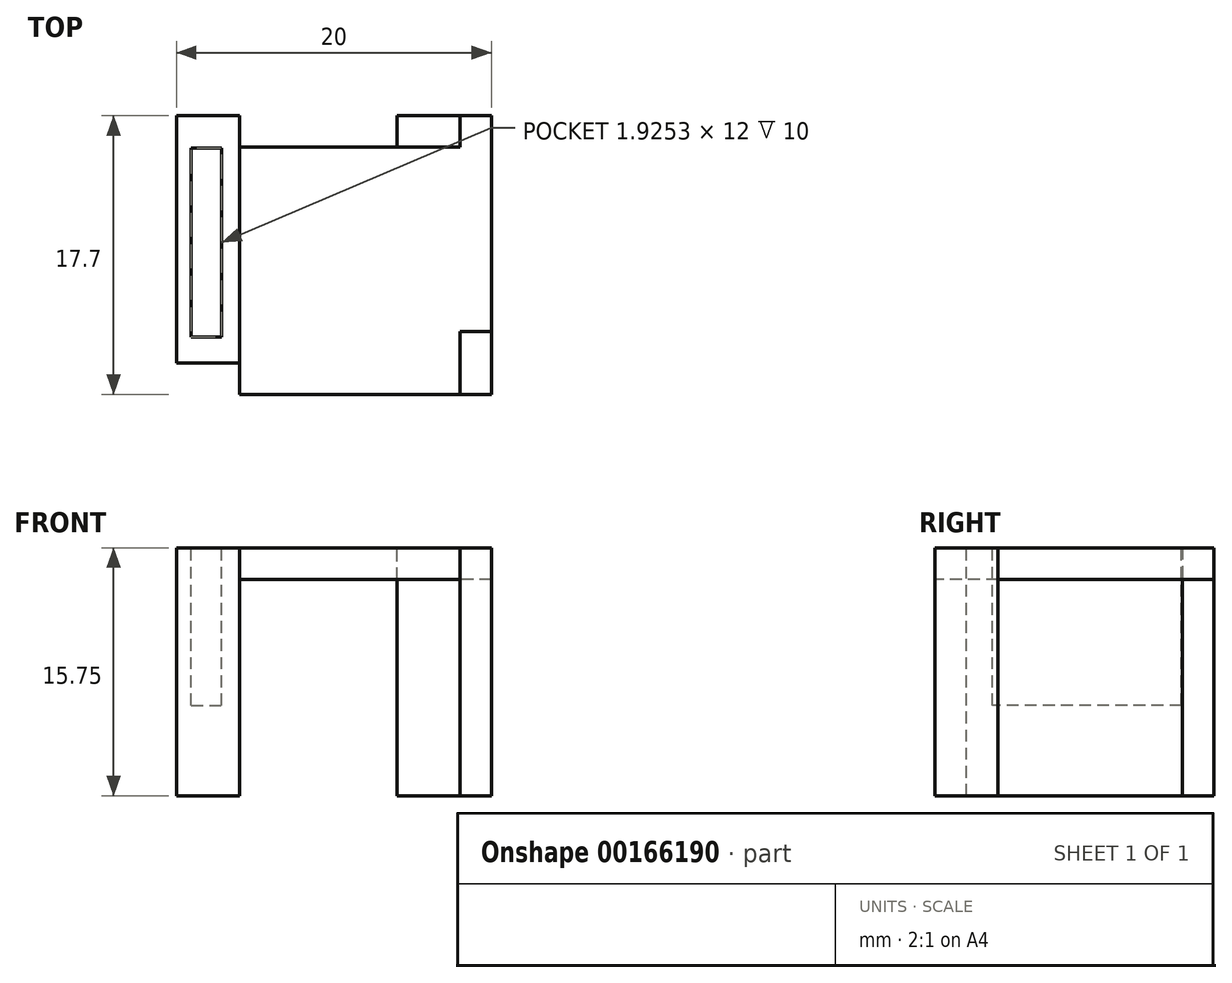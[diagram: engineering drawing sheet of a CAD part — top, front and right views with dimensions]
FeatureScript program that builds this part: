
annotation { "Feature Type Name" : "Feature", "Feature Type Description" : "" }
export const myFeature = defineFeature(function(context is Context, id is Id, definition is map)
    precondition{}
    {
        {
            var Q0;
            Q0=qCreatedBy(makeId("Top.planeOp"),FACE);
            var sketch = newSketch(context, id + "F0", { "sketchPlane" : qUnion([Q0])});
            skLineSegment(sketch, "E0", {"start": v(41.87, -13.52) * mm, "end": v(43.87, -13.52) * mm});
            skLineSegment(sketch, "E1", {"start": v(43.87, -13.52) * mm, "end": v(43.87, -9.52) * mm});
            skLineSegment(sketch, "E2", {"start": v(43.87, -9.52) * mm, "end": v(41.87, -9.52) * mm});
            skLineSegment(sketch, "E3", {"start": v(41.87, -9.52) * mm, "end": v(41.87, -13.52) * mm});
            skLineSegment(sketch, "E4", {"start": v(43.87, -9.52) * mm, "end": v(43.87, 4.18) * mm});
            skLineSegment(sketch, "E5", {"start": v(43.87, 4.18) * mm, "end": v(41.87, 4.18) * mm});
            skLineSegment(sketch, "E6", {"start": v(41.87, 4.18) * mm, "end": v(41.87, 2.18) * mm});
            skLineSegment(sketch, "E7", {"start": v(41.87, 2.18) * mm, "end": v(27.87, 2.18) * mm});
            skLineSegment(sketch, "E8", {"start": v(41.87, -13.52) * mm, "end": v(27.87, -13.52) * mm});
            skLineSegment(sketch, "E9", {"start": v(27.87, 2.18) * mm, "end": v(27.87, -13.52) * mm});
            skLineSegment(sketch, "E10", {"start": v(41.87, 4.18) * mm, "end": v(37.87, 4.18) * mm});
            skLineSegment(sketch, "E11", {"start": v(37.87, 4.18) * mm, "end": v(37.87, 2.18) * mm});
            skLineSegment(sketch, "E12", {"start": v(37.87, 4.18) * mm, "end": v(23.87, 4.18) * mm});
            skLineSegment(sketch, "E13", {"start": v(27.87, -11.52) * mm, "end": v(23.87, -11.52) * mm});
            skPoint(sketch, "E14.orphan", {"position": v(41.87, -11.52) * mm});
            skLineSegment(sketch, "E15", {"start": v(23.87, -11.52) * mm, "end": v(23.87, 4.18) * mm});
            skLineSegment(sketch, "E16", {"start": v(27.87, 2.18) * mm, "end": v(27.87, 4.18) * mm});
            skLineSegment(sketch, "E17", {"start": v(23.87, 5.8) * mm, "end": v(37.87, 5.8) * mm});
            skLineSegment(sketch, "E18", {"start": v(37.87, 5.8) * mm, "end": v(37.87, 7.8) * mm});
            skLineSegment(sketch, "E19", {"start": v(37.87, 7.8) * mm, "end": v(23.87, 7.8) * mm});
            skLineSegment(sketch, "E20", {"start": v(23.87, 7.8) * mm, "end": v(23.87, 5.8) * mm});
            skSolve(sketch);
        }
        {
            var Q0;
            Q0=makeQuery(id+"F0.imprint","IMPRINT",FACE,{"disambiguationData":[TD([[makeQuery(id+"F0.imprint","IMPRINT",EDGE,{"derivedFrom":sQuery(id+"F0.wireOp",EDGE,"E0")}),1.0]])]});
            extrude(context, id + "F1", {"entities" : qUnion([Q0]), "oppositeDirection" : true, "depth" : 13.75 * mm, "hasSecondDirection" : true, "secondDirectionOppositeDirection" : false, "secondDirectionDepth" : 2 * mm});
        }
        {
            var Q0;
            Q0=makeQuery(id+"F0.imprint","IMPRINT",FACE,{"disambiguationData":[TD([[makeQuery(id+"F0.imprint","IMPRINT",EDGE,{"derivedFrom":sQuery(id+"F0.wireOp",EDGE,"E2")}),-1.0]])]});
            extrude(context, id + "F2", {"entities" : qUnion([Q0]), "depth" : 2 * mm});
        }
        {
            var Q0;
            {var subQ0=sQuery(id+"F0.wireOp",EDGE,"E6");Q0=makeQuery(id+"F0.imprint","IMPRINT",FACE,{"disambiguationData":[TD([[makeQuery(id+"F0.imprint","IMPRINT",EDGE,{"derivedFrom":subQ0}),-1.0]])]});}
            extrude(context, id + "F3", {"entities" : qUnion([Q0]), "oppositeDirection" : true, "depth" : 13.75 * mm, "hasSecondDirection" : true, "secondDirectionOppositeDirection" : false, "secondDirectionDepth" : 2 * mm});
        }
        {
            var Q0;
            {var subQ1=sQuery(id+"F0.wireOp",EDGE,"E13");Q0=makeQuery(id+"F0.imprint","IMPRINT",FACE,{"disambiguationData":[TD([[makeQuery(id+"F0.imprint","IMPRINT",EDGE,{"derivedFrom":subQ1}),-1.0]])]});}
            extrude(context, id + "F4", {"entities" : qUnion([Q0]), "oppositeDirection" : true, "depth" : 13.75 * mm, "hasSecondDirection" : true, "secondDirectionOppositeDirection" : false, "secondDirectionDepth" : 2 * mm});
        }
        {
            var Q0;
            Q0=makeQuery(id+"F4.opExtrude","CAP_FACE",FACE,{"disambiguationData":[OSD([sQuery(id+"F0.wireOp",EDGE,"E9"),sQuery(id+"F0.wireOp",EDGE,"E12"),sQuery(id+"F0.wireOp",EDGE,"E13"),sQuery(id+"F0.wireOp",EDGE,"E15"),sQuery(id+"F0.wireOp",EDGE,"E16")])],"isStart":true});
            var sketch = newSketch(context, id + "F5", { "sketchPlane" : qUnion([Q0])});
            skLineSegment(sketch, "E21", {"start": v(24.81, 2.13) * mm, "end": v(26.74, 2.13) * mm});
            skLineSegment(sketch, "E22", {"start": v(26.74, 2.13) * mm, "end": v(26.74, -9.87) * mm});
            skLineSegment(sketch, "E23", {"start": v(26.74, -9.87) * mm, "end": v(24.81, -9.87) * mm});
            skLineSegment(sketch, "E24", {"start": v(24.81, 2.13) * mm, "end": v(24.81, -9.87) * mm});
            skSolve(sketch);
        }
        {
            var Q0;
            Q0=makeQuery(id+"F5.imprint","IMPRINT",FACE,{"disambiguationData":[TD([[makeQuery(id+"F5.imprint","IMPRINT",EDGE,{"derivedFrom":sQuery(id+"F5.wireOp",EDGE,"E21")}),-1.0]])]});
            extrude(context, id + "F6", {"entities" : qUnion([Q0]), "operationType" : NewBodyOperationType.REMOVE, "oppositeDirection" : true, "depth" : 10 * mm});
        }
    });
